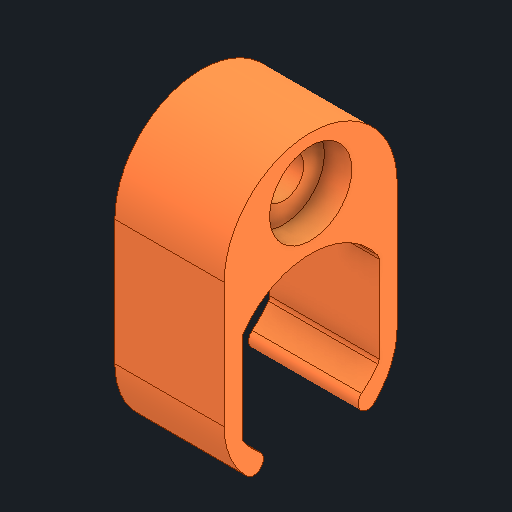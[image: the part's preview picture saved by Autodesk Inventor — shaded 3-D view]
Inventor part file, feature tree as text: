
AUTODESK INVENTOR PART (.ipt)
format: ipt  version: 2023.4 (Build 274418000, 418)  size: 268,288 bytes
history: native  units: mm
features: reference x6, other x4, sketch x2, extrude x2, plane x1, fillet x1, projected_geometry x1
ambient origin geometry x8: Origin, YZ Plane, XZ Plane, XY Plane, X Axis, Y Axis, Z Axis, Center Point
bodies: Solid1 (feature_tree)
feature tree (17):
  sketch  "Sketch1"  dims[d0=1.25mm d1=45.0deg d2=3.0mm]
  plane  "Work Plane1"
  extrude  "Extrusion1"  TaperAngle=45.0deg  [1 undecoded]
  fillet  "Fillet1"  Radius=3.0mm
  extrude  "Extrusion2"  Depth=6.0mm TaperAngle=0.0deg
  reference  "Reference1"
  reference  "Reference2"
  reference  "Reference3"
  reference  "Reference4"
  reference  "Reference5"
  reference  "Reference6"
  sketch  "Sketch2"  dims[d3=6.0mm d4=6.0mm d5=0.0mm d6=0.7mm d7=6.0mm d8=2.0mm d9=0.0mm]
  projected_geometry  "Projected Loop1"
  parser-record x1  (decoder bookkeeping rows leaked as tree rows — omitted from the tree; the rows remain in map.json)
  other  "XYZ Stage V5.iam"
  other  "Y Stage Body v5:1"
  other  "DC Motor:3"
note: 1 required parameter value undecoded (feature->parameter linkage not recoverable at this tier; creation-order binding heuristic only, values carry confidence <= 0.55)
note: 1 file-system path scrubbed to <path> (originals preserved in map.json)
